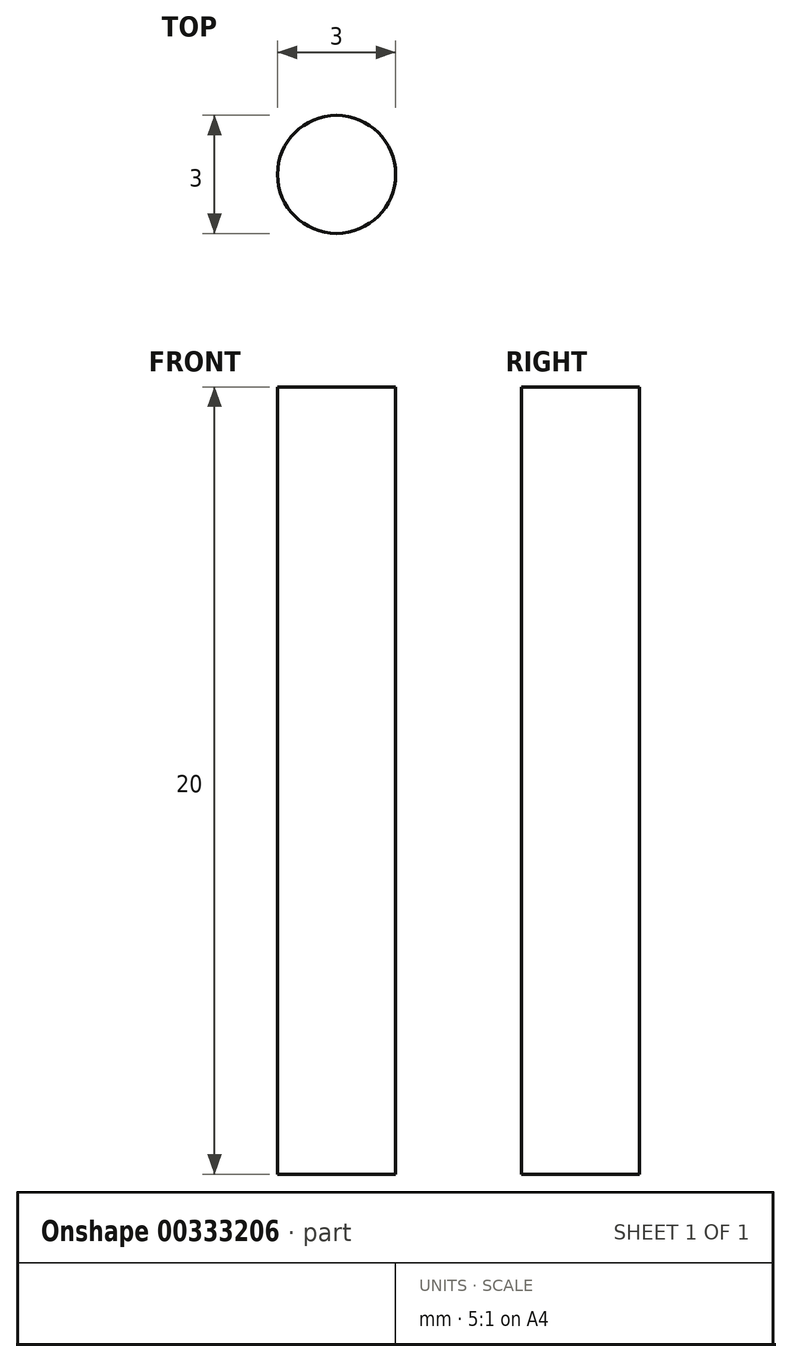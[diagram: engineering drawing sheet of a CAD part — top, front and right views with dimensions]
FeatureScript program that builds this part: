
annotation { "Feature Type Name" : "Feature", "Feature Type Description" : "" }
export const myFeature = defineFeature(function(context is Context, id is Id, definition is map)
    precondition{}
    {
        {
            var Q0;
            Q0=qCreatedBy(makeId("Top.planeOp"),FACE);
            var sketch = newSketch(context, id + "F0", { "sketchPlane" : qUnion([Q0])});
            skCircle(sketch, "E0", {"center": v(0, 0) * mm, "radius": 1.5 * mm});
            skSolve(sketch);
        }
        {
            var Q0;
            Q0=qSketchRegion(id+"F0",true);
            extrude(context, id + "F1", {"entities" : qUnion([Q0]), "depth" : 20 * mm});
        }
    });
